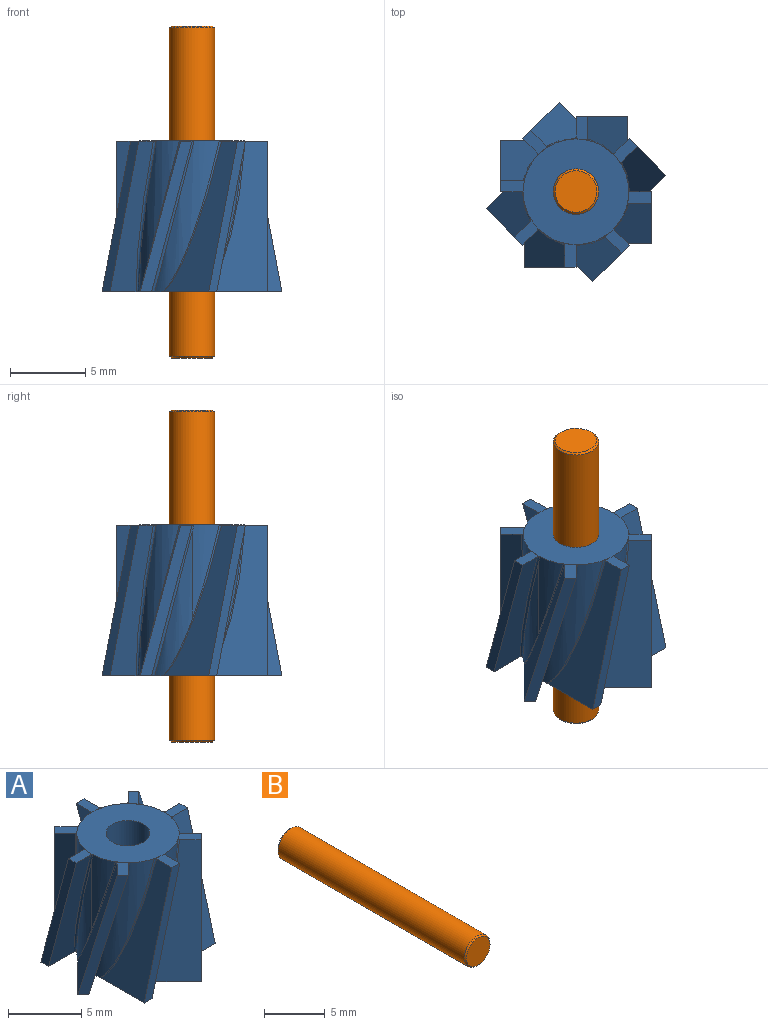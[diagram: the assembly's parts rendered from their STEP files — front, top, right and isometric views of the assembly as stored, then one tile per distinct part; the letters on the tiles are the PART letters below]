
ASSEMBLY  parts=2 mates=2
PART A: 53 faces, bbox 11.9x11.9x12.4 mm
  f0: plane 7x7mm, normal (0,0,1), area 31.4mm2, adj f2,f4
  f1: plane 11.92x11.92mm, normal (0,0,-1), area 51.7mm2, adj f2,f3,f4,f5,f6,f8,f9,f10
  f2: cylinder r=3.5mm len=10mm, axis (0,0,-1), area 113.8mm2, adj f0,f1,f3,f7,f11,f15,f19,f23
  f3: cylinder r=3.5mm len=9.59mm, axis (0,0,-1), area 9.3mm2, adj f1,f2,f46,f47
  f4: cylinder r=1.5mm len=10mm, axis (0,0,-1), area 94.2mm2, adj f0,f1
  f5: plane 9.99x4.26mm, normal (0.97,0,0.26), area 24.1mm2, adj f1,f7,f8,f41
  f6: plane 9.99x2.68mm, normal (-0.97,0,-0.26), area 17.5mm2, adj f1,f7,f8,f42
  f7: plane 1.62x0.99mm, normal (0,0,1), area 1.2mm2, adj f2,f5,f6,f8,f41,f42
  f8: plane 9.99x3.43mm, normal (0,1,0), area 7.5mm2, adj f1,f5,f6,f7
  f9: plane 9.99x4.9mm, normal (0.68,-0.68,0.26), area 24.1mm2, adj f1,f11,f12,f39
  f10: plane 9.99x3.61mm, normal (-0.68,0.68,-0.26), area 17.5mm2, adj f1,f11,f12,f40
  f11: plane 1.75x1.69mm, normal (0,0,1), area 1.2mm2, adj f2,f9,f10,f12,f39,f40
  f12: plane 9.99x2.42mm, normal (0.71,0.71,0), area 7.5mm2, adj f1,f9,f10,f11
  f13: plane 9.99x4.26mm, normal (0,-0.97,0.26), area 24.1mm2, adj f1,f15,f16,f37
  f14: plane 9.99x2.68mm, normal (0,0.97,-0.26), area 17.5mm2, adj f1,f15,f16,f38
  f15: plane 1.62x0.99mm, normal (0,0,1), area 1.2mm2, adj f2,f13,f14,f16,f37,f38
  f16: plane 9.99x3.43mm, normal (1,0,0), area 7.5mm2, adj f1,f13,f14,f15
  f17: plane 9.99x4.9mm, normal (-0.68,-0.68,0.26), area 24.1mm2, adj f1,f19,f20,f50
  f18: plane 9.99x3.61mm, normal (0.68,0.68,-0.26), area 17.5mm2, adj f1,f19,f20,f52
  f19: plane 1.75x1.69mm, normal (0,0,1), area 1.2mm2, adj f2,f17,f18,f20,f50,f52
  f20: plane 9.99x2.42mm, normal (0.71,-0.71,0), area 7.5mm2, adj f1,f17,f18,f19
  f21: plane 9.99x4.26mm, normal (-0.97,0,0.26), area 24.1mm2, adj f1,f23,f24,f49
  f22: plane 9.99x2.68mm, normal (0.97,0,-0.26), area 17.5mm2, adj f1,f23,f24,f51
  f23: plane 1.62x0.99mm, normal (0,0,1), area 1.2mm2, adj f2,f21,f22,f24,f49,f51
  f24: plane 9.99x3.43mm, normal (0,-1,0), area 7.5mm2, adj f1,f21,f22,f23
  f25: plane 9.99x4.9mm, normal (-0.68,0.68,0.26), area 24.1mm2, adj f1,f27,f28,f47
  f26: plane 9.99x3.61mm, normal (0.68,-0.68,-0.26), area 17.5mm2, adj f1,f27,f28,f48
  f27: plane 1.75x1.69mm, normal (0,0,1), area 1.2mm2, adj f2,f25,f26,f28,f47,f48
  f28: plane 9.99x2.42mm, normal (-0.71,-0.71,0), area 7.5mm2, adj f1,f25,f26,f27
  f29: plane 9.99x4.26mm, normal (0,0.97,0.26), area 24.1mm2, adj f1,f31,f32,f45
  f30: plane 9.99x2.68mm, normal (0,-0.97,-0.26), area 17.5mm2, adj f1,f31,f32,f46
  f31: plane 1.62x0.99mm, normal (0,0,1), area 1.2mm2, adj f2,f29,f30,f32,f45,f46
  f32: plane 9.99x3.43mm, normal (-1,0,0), area 7.5mm2, adj f1,f29,f30,f31
  f33: plane 9.99x4.9mm, normal (0.68,0.68,0.26), area 24.1mm2, adj f1,f35,f36,f43
  f34: plane 9.99x3.61mm, normal (-0.68,-0.68,-0.26), area 17.5mm2, adj f1,f35,f36,f44
  f35: plane 1.75x1.69mm, normal (0,0,1), area 1.2mm2, adj f2,f33,f34,f36,f43,f44
  f36: plane 9.99x2.42mm, normal (-0.71,0.71,0), area 7.5mm2, adj f1,f33,f34,f35
  f37: bspline ~10.06x2.84mm, area 1.2mm2, adj f1,f2,f13,f15
  f38: bspline ~10.07x2.81mm, area 2.5mm2, adj f1,f2,f14,f15
  f39: bspline ~10.06x3.91mm, area 1.2mm2, adj f1,f2,f9,f11
  f40: bspline ~12.37x3.32mm, area 2.5mm2, adj f1,f2,f10,f11
  f41: bspline ~10.06x2.84mm, area 1.2mm2, adj f1,f2,f5,f7
  f42: bspline ~10.07x2.81mm, area 2.5mm2, adj f1,f2,f6,f7
  f43: bspline ~10.06x3.91mm, area 1.2mm2, adj f1,f2,f33,f35
  f44: bspline ~12.37x3.32mm, area 2.5mm2, adj f1,f2,f34,f35
  f45: bspline ~10.06x2.84mm, area 1.2mm2, adj f1,f2,f29,f31
  f46: bspline ~10.07x2.81mm, area 2.5mm2, adj f1,f2,f3,f30,f31
  f47: bspline ~10.06x3.91mm, area 1.2mm2, adj f1,f2,f3,f25,f27
  f48: bspline ~12.37x3.32mm, area 2.5mm2, adj f1,f2,f26,f27
  f49: bspline ~10.06x2.84mm, area 1.2mm2, adj f1,f2,f21,f23
  f50: bspline ~10.06x3.91mm, area 1.2mm2, adj f1,f2,f17,f19
  f51: bspline ~10.07x2.81mm, area 2.5mm2, adj f1,f2,f22,f23
  f52: bspline ~12.37x3.32mm, area 2.5mm2, adj f1,f2,f18,f19
PART B: 5 faces, bbox 3x22x3 mm
  f0: cylinder r=1.5mm len=21.76mm, axis (0,-1,0), area 205.1mm2, adj f3,f4
  f1: plane 2.76x2.76mm, normal (0,1,0), area 6mm2, adj f4
  f2: plane 2.76x2.76mm, normal (0,-1,0), area 6mm2, adj f3
  f3: cone r=1.5mm half-angle=45deg, axis (0,1,0), area 1.5mm2, adj f0,f2
  f4: cone r=1.38mm half-angle=45deg, axis (0,-1,0), area 1.5mm2, adj f0,f1
PLACE A t=(-1.55,5.92,-6.61)mm
PLACE B rot(axis=(1,0,0),90deg) t=(-1.55,5.92,-4.99)mm
MATE cylindrical B.f0 <-> A.f2  axis (0,0,-1) through (-1.55,5.92,-4.99)mm
MATE fastened A.f2 <-> B.f0  axis (0,0,1) through (-1.55,5.92,-1.61)mm
